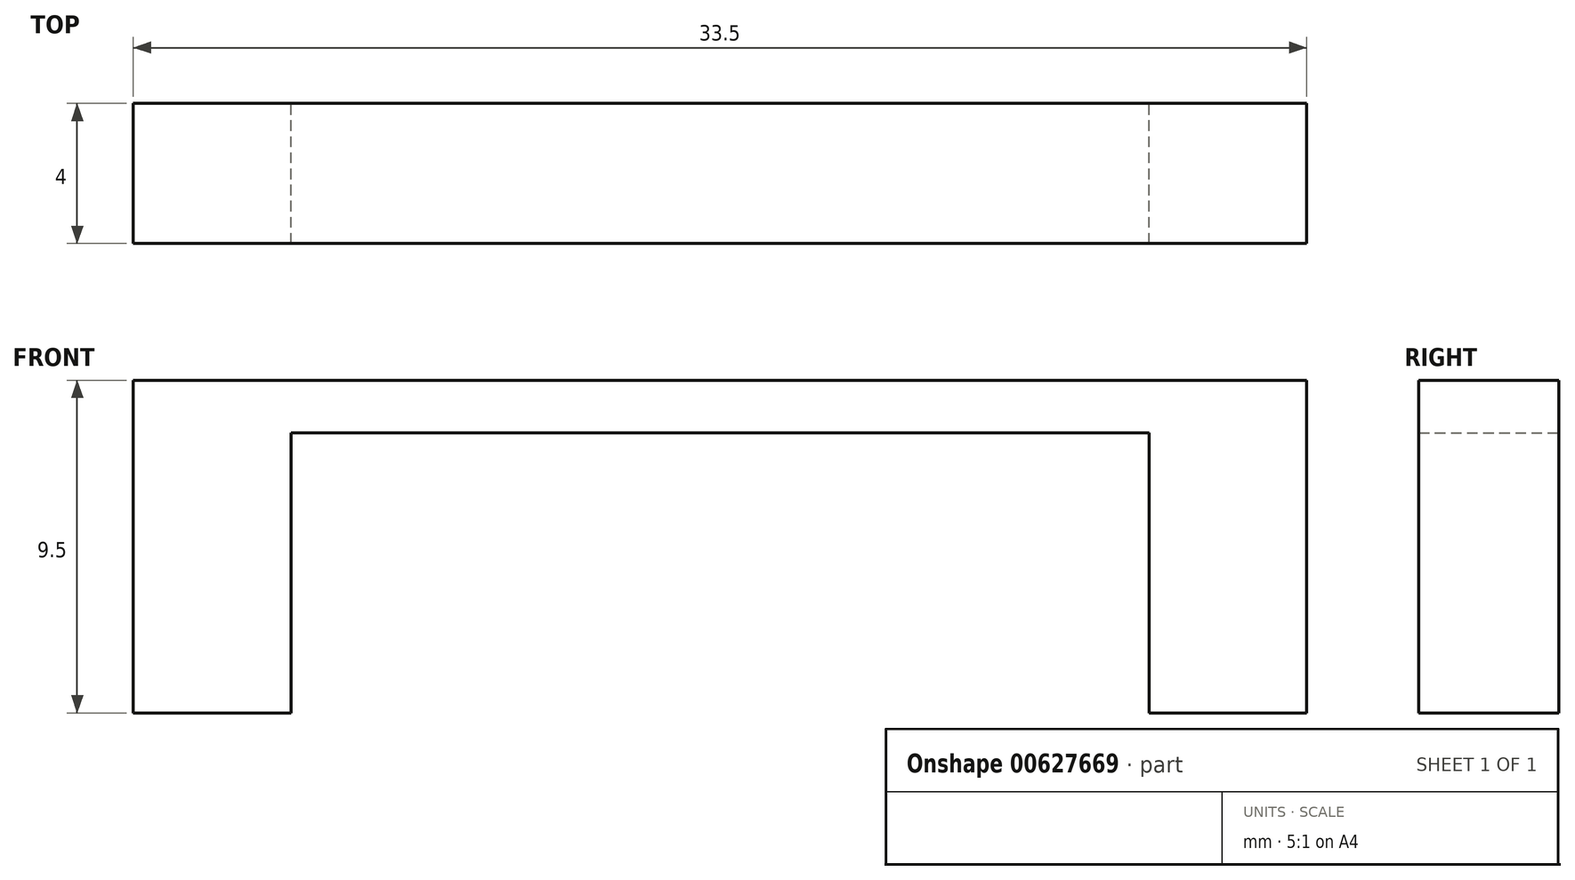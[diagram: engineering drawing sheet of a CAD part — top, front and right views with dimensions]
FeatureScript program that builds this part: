
annotation { "Feature Type Name" : "Feature", "Feature Type Description" : "" }
export const myFeature = defineFeature(function(context is Context, id is Id, definition is map)
    precondition{}
    {
        {
            var Q0;
            Q0=qCreatedBy(makeId("Front.planeOp"),FACE);
            var sketch = newSketch(context, id + "F0", { "sketchPlane" : qUnion([Q0])});
            skLineSegment(sketch, "E0", {"start": v(0, 8) * mm, "end": v(24.5, 8) * mm});
            skLineSegment(sketch, "E1", {"start": v(0, 0) * mm, "end": v(0, 8) * mm});
            skLineSegment(sketch, "E2", {"start": v(24.5, 8) * mm, "end": v(24.5, 0) * mm});
            skLineSegment(sketch, "E3.0", {"start": v(29, 9.5) * mm, "end": v(29, 0) * mm});
            skLineSegment(sketch, "E3.2", {"start": v(-4.5, 0) * mm, "end": v(-4.5, 9.5) * mm});
            skLineSegment(sketch, "E4", {"start": v(-4.5, 0) * mm, "end": v(0, 0) * mm});
            skLineSegment(sketch, "E5", {"start": v(24.5, 0) * mm, "end": v(29, 0) * mm});
            skLineSegment(sketch, "E6", {"start": v(-4.5, 9.5) * mm, "end": v(29, 9.5) * mm});
            skSolve(sketch);
        }
        {
            var Q0;
            Q0 = qSketchRegion(id + "F0", true);
            extrude(context, id + "F1", {"entities" : qUnion([Q0]), "depth" : 4 * mm, "offsetDistance" : 25 * mm});
        }
    });
